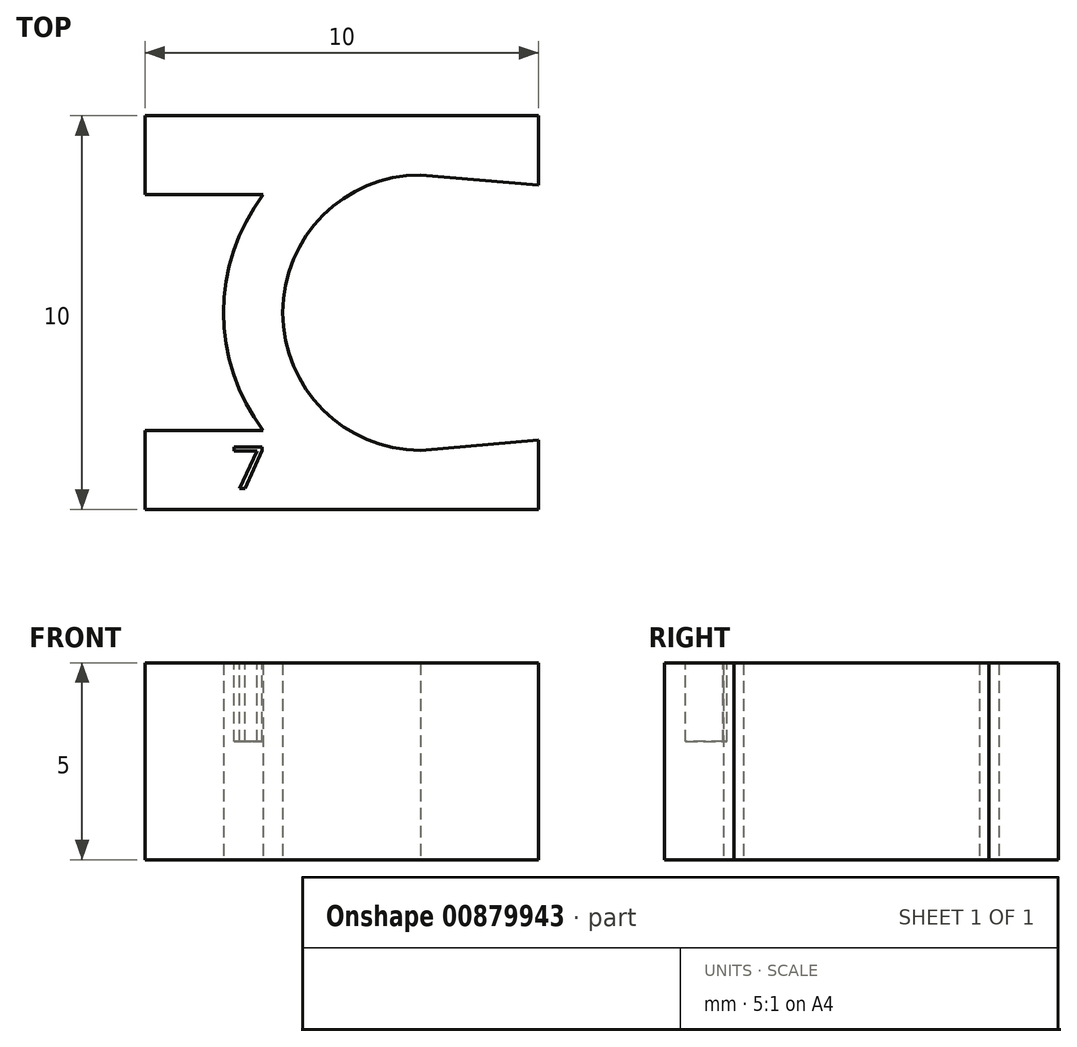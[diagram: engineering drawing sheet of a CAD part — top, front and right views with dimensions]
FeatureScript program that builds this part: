
annotation { "Feature Type Name" : "Feature", "Feature Type Description" : "" }
export const myFeature = defineFeature(function(context is Context, id is Id, definition is map)
    precondition{}
    {
        {
            var Q0;
            Q0=qCreatedBy(makeId("Top.planeOp"),FACE);
            var sketch = newSketch(context, id + "F0", { "sketchPlane" : qUnion([Q0])});
            skArc(sketch, "E0", {"start": v(0, 3.5) * mm, "mid": v(-3.5, 0) * mm, "end": v(0, -3.5) * mm});
            skArc(sketch, "E1", {"start": v(-4, 3) * mm, "mid": v(-5, 0) * mm, "end": v(-4, -3) * mm});
            skLineSegment(sketch, "E2", {"start": v(0, -5) * mm, "end": v(3, -5) * mm});
            skLineSegment(sketch, "E3", {"start": v(0, 5) * mm, "end": v(3, 5) * mm});
            skLineSegment(sketch, "E4", {"start": v(0, 3.5) * mm, "end": v(3, 3.24) * mm});
            skLineSegment(sketch, "E5", {"start": v(0, -3.5) * mm, "end": v(3, -3.24) * mm});
            skLineSegment(sketch, "E6", {"start": v(3, -3.24) * mm, "end": v(3, -5) * mm});
            skLineSegment(sketch, "E7", {"start": v(3, 5) * mm, "end": v(3, 3.24) * mm});
            skLineSegment(sketch, "E8", {"start": v(0, 5) * mm, "end": v(-7, 5) * mm});
            skLineSegment(sketch, "E9", {"start": v(-4, 3) * mm, "end": v(-7, 3) * mm});
            skLineSegment(sketch, "E10", {"start": v(0, -5) * mm, "end": v(-7, -5) * mm});
            skLineSegment(sketch, "E11", {"start": v(-4, -3) * mm, "end": v(-7, -3) * mm});
            skLineSegment(sketch, "E12", {"start": v(-7, -3) * mm, "end": v(-7, -5) * mm});
            skLineSegment(sketch, "E13", {"start": v(-7, 5) * mm, "end": v(-7, 3) * mm});
            skSolve(sketch);
        }
        {
            var Q0;
            Q0=makeQuery(id+"F0.imprint","IMPRINT",FACE,{"disambiguationData":[TD([[makeQuery(id+"F0.imprint","IMPRINT",EDGE,{"derivedFrom":sQuery(id+"F0.wireOp",EDGE,"E0")}),-1.0]])]});
            extrude(context, id + "F1", {"entities" : qUnion([Q0]), "depth" : 5 * mm, "offsetDistance" : 25 * mm});
        }
        {
            var Q0;
            Q0=makeQuery(id+"F1.opExtrude","CAP_FACE",FACE,{"disambiguationData":[OSD([sQuery(id+"F0.wireOp",EDGE,"E0"),sQuery(id+"F0.wireOp",EDGE,"E1"),sQuery(id+"F0.wireOp",EDGE,"E2"),sQuery(id+"F0.wireOp",EDGE,"E3"),sQuery(id+"F0.wireOp",EDGE,"E4"),sQuery(id+"F0.wireOp",EDGE,"E5"),sQuery(id+"F0.wireOp",EDGE,"E6"),sQuery(id+"F0.wireOp",EDGE,"E7"),sQuery(id+"F0.wireOp",EDGE,"E8"),sQuery(id+"F0.wireOp",EDGE,"E9"),sQuery(id+"F0.wireOp",EDGE,"E10"),sQuery(id+"F0.wireOp",EDGE,"E11"),sQuery(id+"F0.wireOp",EDGE,"E12"),sQuery(id+"F0.wireOp",EDGE,"E13")])],"isStart":false});
            var sketch = newSketch(context, id + "F2", { "sketchPlane" : qUnion([Q0])});
            skText(sketch, "E14", { "text": "7", "fontName": "OpenSans-Regular.ttf"});
            const initialGuessF2  = {"E14": [-0.0048, -0.00447, 1, 0, 0.00107]};
            skSetInitialGuess(sketch, initialGuessF2);
            skSolve(sketch);
        }
        {
            var Q0;
            Q0=makeQuery(id+"F2.imprint","IMPRINT",FACE,{"disambiguationData":[TD([[makeQuery(id+"F2.imprint","IMPRINT",EDGE,{"derivedFrom":sQuery(id+"F2.wireOp",EDGE,"E14.sketch_text.stroke-0")}),-1.0]])]});
            extrude(context, id + "F3", {"entities" : qUnion([Q0]), "operationType" : NewBodyOperationType.REMOVE, "oppositeDirection" : true, "depth" : 2 * mm, "offsetDistance" : 25 * mm});
        }
    });
